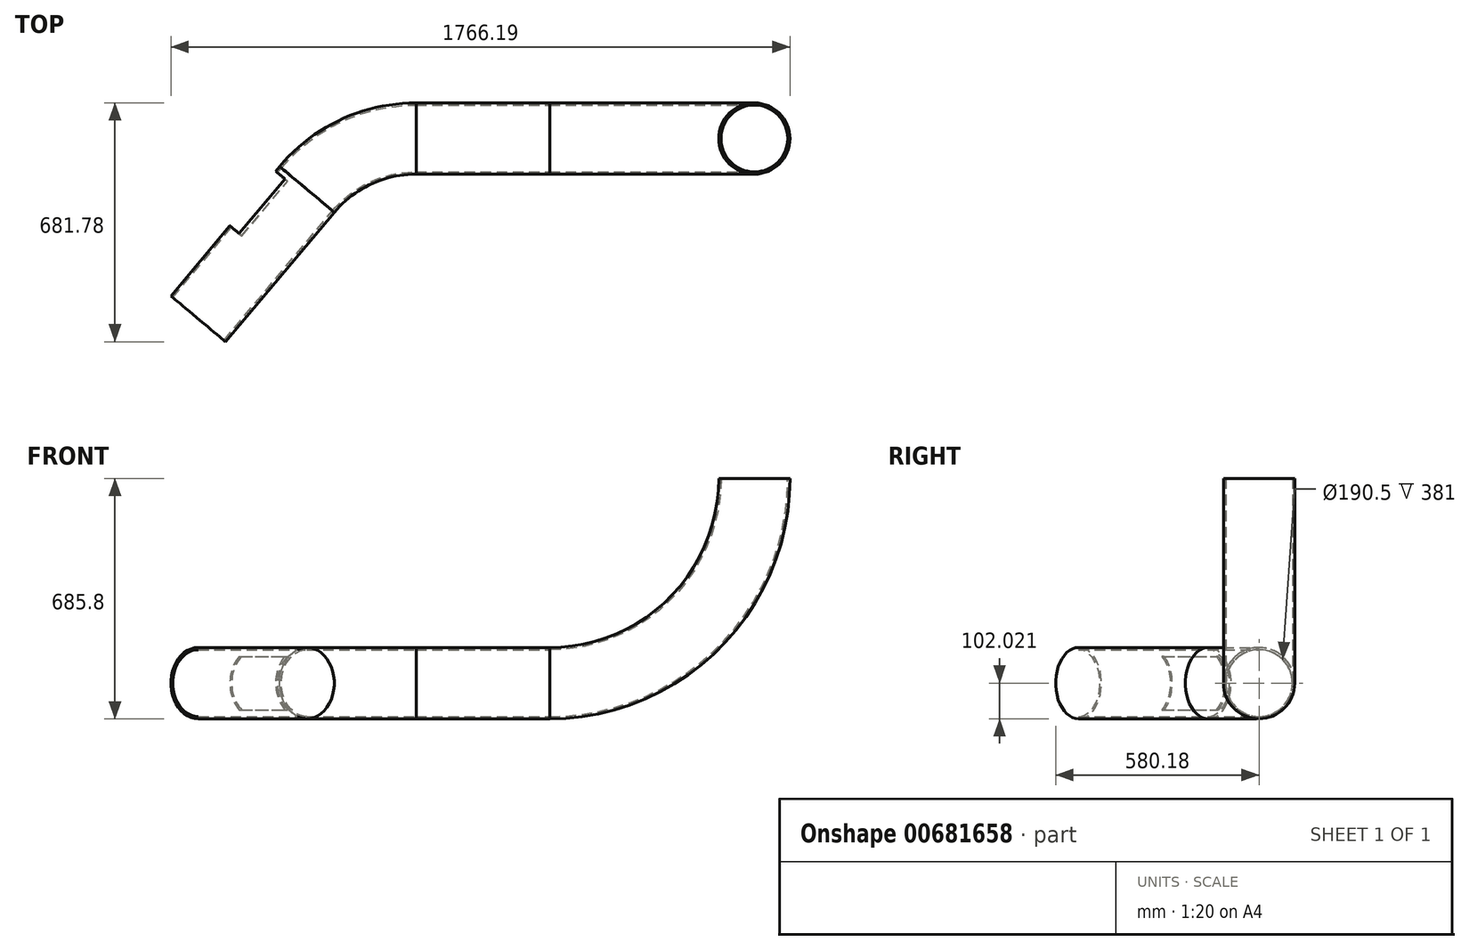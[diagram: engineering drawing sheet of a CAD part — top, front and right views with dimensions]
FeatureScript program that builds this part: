
annotation { "Feature Type Name" : "Feature", "Feature Type Description" : "" }
export const myFeature = defineFeature(function(context is Context, id is Id, definition is map)
    precondition{}
    {
        {
            var Q0;
            Q0=qCreatedBy(makeId("Top.planeOp"),FACE);
            var sketch = newSketch(context, id + "F0", { "sketchPlane" : qUnion([Q0])});
            skCircle(sketch, "E0", {"center": v(0, 0) * mm, "radius": 101.6 * mm});
            skCircle(sketch, "E1", {"center": v(0, 0) * mm, "radius": 95.25 * mm});
            skLineSegment(sketch, "E2", {"start": v(0, 0) * mm, "end": v(-762, 0) * mm, "construction": true});
            skLineSegment(sketch, "E3", {"start": v(-584.2, 0) * mm, "end": v(-584.2, -420.9) * mm, "construction": true});
            skSolve(sketch);
        }
        {
            var Q0;
            Q0=qCreatedBy(makeId("Front.planeOp"),FACE);
            var sketch = newSketch(context, id + "F1", { "sketchPlane" : qUnion([Q0])});
            skLineSegment(sketch, "E4.bottom", {"start": v(0, 0) * mm, "end": v(-584.2, 0) * mm, "construction": true});
            skLineSegment(sketch, "E4.top", {"start": v(0, -584.2) * mm, "end": v(-584.2, -584.2) * mm, "construction": true});
            skLineSegment(sketch, "E4.left", {"start": v(0, 0) * mm, "end": v(0, -584.2) * mm, "construction": true});
            skLineSegment(sketch, "E4.right", {"start": v(-584.2, 0) * mm, "end": v(-584.2, -584.2) * mm, "construction": true});
            skLineSegment(sketch, "E5", {"start": v(-584.2, -584.2) * mm, "end": v(-1346.2, -584.2) * mm, "construction": true});
            skSolve(sketch);
        }
        {
            var Q0;
            Q0=sQuery(id+"F1.wireOp",EDGE,"E4.right");
            cPlane(context, id + "F2", {"entities" : qUnion([Q0]), "cplaneType" : CPlaneType.LINE_ANGLE, "offset" : 25.4 * mm, "angle" : 0 * degree, "width" : 152.4 * mm, "height" : 152.4 * mm});
        }
        {
            var Q0;
            Q0=makeQuery(id+"F0.imprint","IMPRINT",FACE,{"disambiguationData":[TD([[makeQuery(id+"F0.imprint","IMPRINT",EDGE,{"derivedFrom":sQuery(id+"F0.wireOp",EDGE,"E0")}),1.0]])]});
            var Q1;
            Q1=sQuery(id+"F0.wireOp",EDGE,"E3");
            revolve(context, id + "F3", {"surfaceOperationType" : NewSurfaceOperationType.NEW, "entities" : qUnion([Q0]), "axis" : qUnion([Q1]), "revolveType" : RevolveType.ONE_DIRECTION, "oppositeDirection" : true, "angle" : 90 * degree});
        }
        {
            var Q0;
            Q0=qCreatedBy(id+"F2.planeOp",FACE);
            var sketch = newSketch(context, id + "F4", { "sketchPlane" : qUnion([Q0])});
            skCircle(sketch, "E6", {"center": v(0, -583.78) * mm, "radius": 101.6 * mm});
            skCircle(sketch, "E7", {"center": v(0, -583.78) * mm, "radius": 95.25 * mm});
            skSolve(sketch);
        }
        {
            var Q0;
            Q0=makeQuery(id+"F4.imprint","IMPRINT",FACE,{"disambiguationData":[TD([[makeQuery(id+"F4.imprint","IMPRINT",EDGE,{"derivedFrom":sQuery(id+"F4.wireOp",EDGE,"E6")}),1.0]])]});
            extrude(context, id + "F5", {"entities" : qUnion([Q0]), "operationType" : NewBodyOperationType.ADD, "depth" : 381 * mm, "offsetDistance" : 25.4 * mm});
        }
        {
            var Q0;
            Q0=sQuery(id+"F1.wireOp",EDGE,"E4.top");
            cPlane(context, id + "F6", {"entities" : qUnion([Q0]), "cplaneType" : CPlaneType.LINE_ANGLE, "offset" : 25.4 * mm, "angle" : 90 * degree, "width" : 152.4 * mm, "height" : 152.4 * mm});
        }
        {
            var Q0;
            Q0=qCreatedBy(id+"F6.planeOp",FACE);
            var sketch = newSketch(context, id + "F7", { "sketchPlane" : qUnion([Q0])});
            skLineSegment(sketch, "E8", {"start": v(-965.2, 0) * mm, "end": v(-965.2, -609.6) * mm, "construction": true});
            skArc(sketch, "E9", {"start": v(-965.2, 0) * mm, "mid": v(-1136.95, -38.08) * mm, "end": v(-1276.52, -145.17) * mm, "construction": true});
            skArc(sketch, "E10", {"start": v(-965.2, -101.6) * mm, "mid": v(-1094.34, -130.3) * mm, "end": v(-1199.15, -211.02) * mm, "construction": true});
            skArc(sketch, "E11", {"start": v(-965.2, 101.6) * mm, "mid": v(-1179.9, 54) * mm, "end": v(-1354.35, -79.86) * mm, "construction": true});
            skLineSegment(sketch, "E12", {"start": v(-965.2, -406.4) * mm, "end": v(-1354.35, -79.86) * mm, "construction": true});
            skLineSegment(sketch, "E13", {"start": v(-1276.52, -145.17) * mm, "end": v(-1586.73, -514.86) * mm, "construction": true});
            skSolve(sketch);
        }
        {
            var Q0;
            Q0=sQuery(id+"F7.wireOp",EDGE,"E8");
            cPlane(context, id + "F8", {"entities" : qUnion([Q0]), "cplaneType" : CPlaneType.LINE_ANGLE, "offset" : 25.4 * mm, "angle" : 90 * degree, "width" : 152.4 * mm, "height" : 152.4 * mm});
        }
        {
            var Q0;
            Q0=qCreatedBy(id+"F8.planeOp",FACE);
            var sketch = newSketch(context, id + "F9", { "sketchPlane" : qUnion([Q0])});
            skLineSegment(sketch, "E14", {"start": v(-406.44, -584.23) * mm, "end": v(-406.44, -279.43) * mm, "construction": true});
            skCircle(sketch, "E15", {"center": v(0, -583.98) * mm, "radius": 101.6 * mm});
            skCircle(sketch, "E16", {"center": v(0, -583.98) * mm, "radius": 95.25 * mm});
            skSolve(sketch);
        }
        {
            var Q0;
            Q0=makeQuery(id+"F9.imprint","IMPRINT",FACE,{"disambiguationData":[TD([[makeQuery(id+"F9.imprint","IMPRINT",EDGE,{"derivedFrom":sQuery(id+"F9.wireOp",EDGE,"E15")}),1.0]])]});
            var Q1;
            Q1=sQuery(id+"F9.wireOp",EDGE,"E14");
            revolve(context, id + "F10", {"surfaceOperationType" : NewSurfaceOperationType.NEW, "entities" : qUnion([Q0]), "axis" : qUnion([Q1]), "revolveType" : RevolveType.ONE_DIRECTION, "angle" : 50 * degree});
        }
        {
            var Q0;
            Q0=sQuery(id+"F7.wireOp",EDGE,"E12");
            cPlane(context, id + "F11", {"entities" : qUnion([Q0]), "cplaneType" : CPlaneType.LINE_ANGLE, "offset" : 25.4 * mm, "angle" : 0 * degree, "width" : 152.4 * mm, "height" : 152.4 * mm});
        }
        {
            var Q0;
            Q0=makeQuery(id+"F10.opRevolve","CAP_FACE",FACE,{"disambiguationData":[OSD([sQuery(id+"F9.wireOp",EDGE,"E15"),sQuery(id+"F9.wireOp",EDGE,"E16")])],"isStart":false});
            extrude(context, id + "F12", {"entities" : qUnion([Q0]), "depth" : 482.6 * mm, "offsetDistance" : 25.4 * mm});
        }
        {
            var Q0;
            Q0=sQuery(id+"F7.wireOp",EDGE,"E13");
            cPlane(context, id + "F13", {"entities" : qUnion([Q0]), "cplaneType" : CPlaneType.LINE_ANGLE, "offset" : 25.4 * mm, "angle" : 90 * degree, "width" : 152.4 * mm, "height" : 152.4 * mm});
        }
        {
            var Q0;
            Q0=qCreatedBy(id+"F13.planeOp",FACE);
            var sketch = newSketch(context, id + "F14", { "sketchPlane" : qUnion([Q0])});
            skLineSegment(sketch, "E17", {"start": v(-1406.72, -584.19) * mm, "end": v(-1051.12, -584.19) * mm, "construction": true});
            skLineSegment(sketch, "E18.bottom", {"start": v(-1152.72, -507.99) * mm, "end": v(-949.52, -507.99) * mm});
            skLineSegment(sketch, "E18.top", {"start": v(-1152.72, -660.39) * mm, "end": v(-949.52, -660.39) * mm});
            skLineSegment(sketch, "E18.left", {"start": v(-1152.72, -507.99) * mm, "end": v(-1152.72, -660.39) * mm});
            skLineSegment(sketch, "E18.right", {"start": v(-949.52, -507.99) * mm, "end": v(-949.52, -660.39) * mm});
            skPoint(sketch, "E18.middle", {"position": v(-1051.12, -584.19) * mm});
            skSolve(sketch);
        }
        {
            var Q0;
            Q0=makeQuery(id+"F14.imprint","IMPRINT",FACE,{"disambiguationData":[TD([[makeQuery(id+"F14.imprint","IMPRINT",EDGE,{"derivedFrom":sQuery(id+"F14.wireOp",EDGE,"E18.bottom")}),-1.0]])]});
            extrude(context, id + "F15", {"entities" : qUnion([Q0]), "operationType" : NewBodyOperationType.REMOVE, "oppositeDirection" : true, "depth" : 233.93 * mm, "offsetDistance" : 25.4 * mm});
        }
    });
